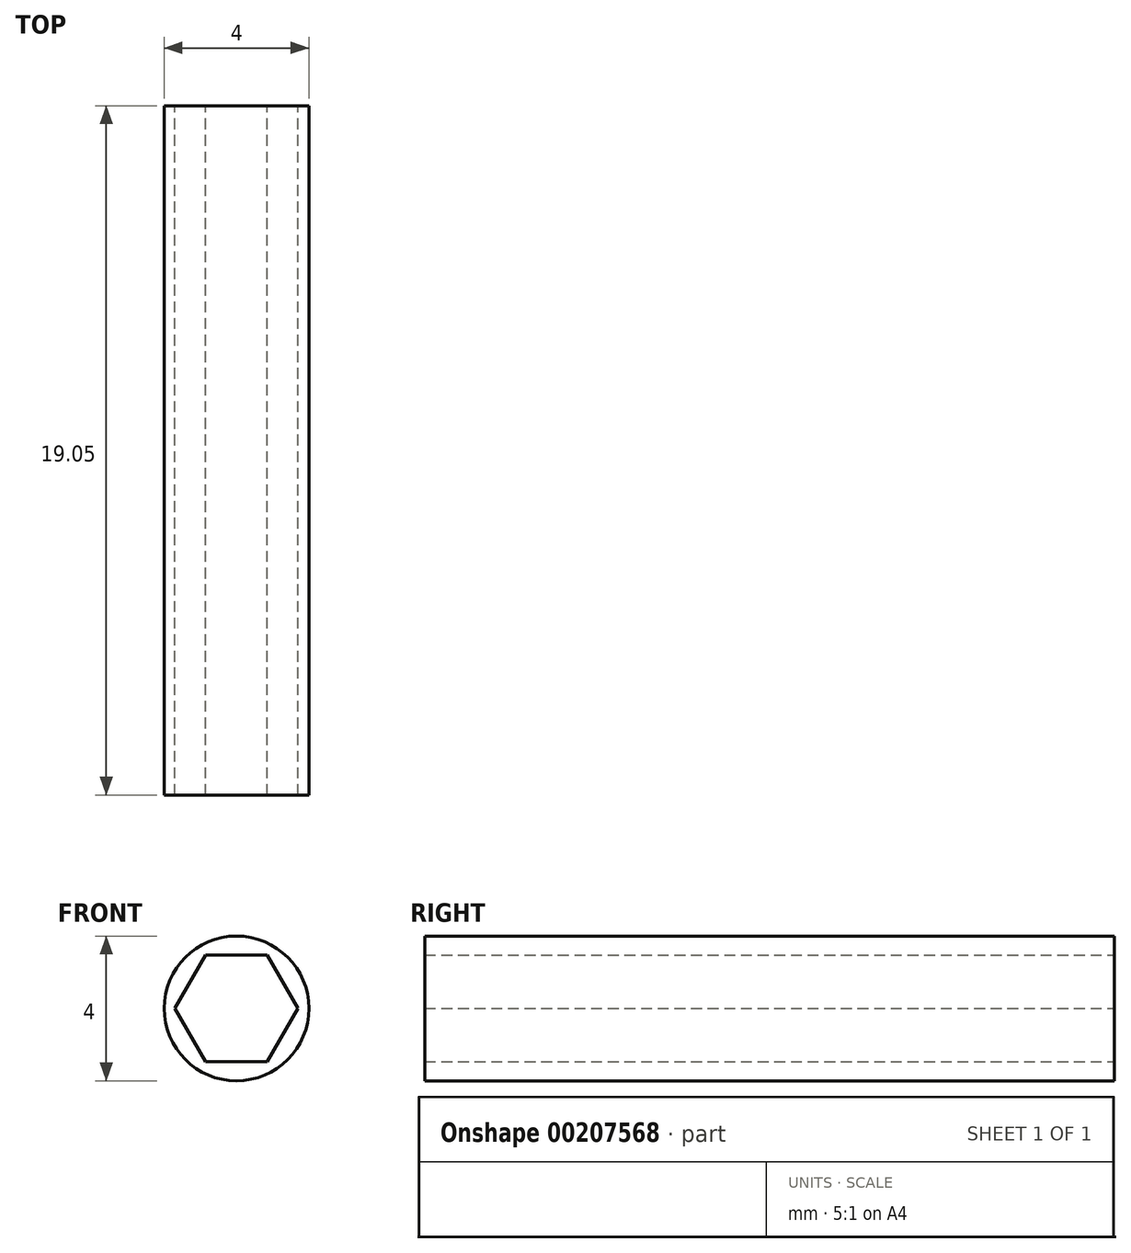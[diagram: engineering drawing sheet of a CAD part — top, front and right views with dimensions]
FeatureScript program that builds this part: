
annotation { "Feature Type Name" : "Feature", "Feature Type Description" : "" }
export const myFeature = defineFeature(function(context is Context, id is Id, definition is map)
    precondition{}
    {
        {
            var Q0;
            Q0=qCreatedBy(makeId("Front.planeOp"),FACE);
            var sketch = newSketch(context, id + "F0", { "sketchPlane" : qUnion([Q0])});
            skCircle(sketch, "E0.cCircle", {"center": v(0, 0) * mm, "radius": 1.48 * mm, "construction": true});
            skLineSegment(sketch, "E0.0", {"start": v(1.7, 0) * mm, "end": v(0.85, -1.48) * mm});
            skLineSegment(sketch, "E0.1", {"start": v(0.85, -1.48) * mm, "end": v(-0.85, -1.48) * mm});
            skLineSegment(sketch, "E0.2", {"start": v(-0.85, -1.47) * mm, "end": v(-1.7, 0) * mm});
            skLineSegment(sketch, "E0.3", {"start": v(-1.7, 0) * mm, "end": v(-0.85, 1.47) * mm});
            skLineSegment(sketch, "E0.4", {"start": v(-0.85, 1.48) * mm, "end": v(0.85, 1.48) * mm});
            skLineSegment(sketch, "E0.5", {"start": v(0.85, 1.47) * mm, "end": v(1.7, 0) * mm});
            skPoint(sketch, "E0.0.midPoint", {"position": v(1.28, -0.74) * mm});
            skLineSegment(sketch, "E1", {"start": v(0, 1.48) * mm, "end": v(0, -1.48) * mm, "construction": true});
            skCircle(sketch, "E2", {"center": v(0, 0) * mm, "radius": 2 * mm});
            skLineSegment(sketch, "E3", {"start": v(-1.7, 0) * mm, "end": v(1.7, 0) * mm, "construction": true});
            skSolve(sketch);
        }
        {
            var Q0;
            Q0=makeQuery(id+"F0.imprint","IMPRINT",FACE,{"disambiguationData":[TD([[makeQuery(id+"F0.imprint","IMPRINT",EDGE,{"derivedFrom":sQuery(id+"F0.wireOp",EDGE,"E0.0")}),1.0]])]});
            extrude(context, id + "F1", {"entities" : qUnion([Q0]), "depth" : 19.05 * mm});
        }
    });
